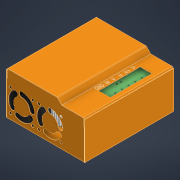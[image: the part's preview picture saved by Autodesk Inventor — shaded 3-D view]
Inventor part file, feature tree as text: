
AUTODESK INVENTOR PART (.ipt)
format: ipt  version: 2022 (Build 260153000, 153)  size: 3,366,912 bytes
history: native  units: in
note: dims shown in document units (in); Inventor stores cm internally (conversion verified against a paired STEP export)
features: other x13, sheet_metal_op x12, sketch x10, plane x2, pattern_linear x2, mirror x1, hole x1, emboss x1, projected_geometry x1
ambient origin geometry x8: Origin, YZ Plane, XZ Plane, XY Plane, X Axis, Y Axis, Z Axis, Center Point
bodies: Solid1 (feature_tree), Solid2 (feature_tree), Solid3 (feature_tree), Solid4 (feature_tree), Solid5 (feature_tree)
feature tree (43):
  other  "Inner Assembly.iam"
  other  "heatsink.ipt:1"
  other  "PCB v1.iam:1::HV servo drive v1 PCB.ipt:1"
  other  "SanAce_9GA_40x20_RBD.ipt:1"
  plane  "Work Plane1"
  sheet_metal_op  "Face1"
  sheet_metal_op  "Flange1"
  sheet_metal_op  "Flange2"
  sketch  "Sketch4"  dims[d4=0.1in]
  sheet_metal_op  "Face3"
  plane  "Work Plane2"
  mirror  "Mirror1"
  sheet_metal_op  "Contour Flange1"
  sketch  "Sketch6"  dims[d6=0.03in]
  hole  "Hole1"  [1 undecoded]
  pattern_linear  "Rectangular Pattern1"  Spacing1=-0.45in  [1 undecoded]
  pattern_linear  "Rectangular Pattern2"  Spacing1=0.12in  [1 undecoded]
  emboss  "Emboss1"
  sketch  "Sketch1"  dims[d0=0.3937in d1=0.06in]
  other  "Plate1"
  sketch  "Sketch2"  dims[d2=0.1in]
  other  "Plate2"
  sheet_metal_op  "Bend1"
  sheet_metal_op  "Corner1"
  sketch  "Sketch3"  dims[d3=1.0in]
  other  "Plate3"
  sheet_metal_op  "Bend2"
  sheet_metal_op  "Corner2"
  other  "Plate5"
  sheet_metal_op  "Bend4"
  sketch  "Sketch5"  dims[d5=0.03in]
  other  "Plate6"
  sheet_metal_op  "Bend5"
  sheet_metal_op  "Corner3"
  sketch  "Sketch7"  dims[d7=0.015in]
  sketch  "Sketch8"  dims[d8=0.06in]
  sketch  "Sketch9"  dims[d9=0.03in]
  projected_geometry  "Projected Loop1"
  sketch  "Sketch10"  dims[d10=1.0in d11=90.0deg d12=0.03in d13=-0.45in d14=0.12in d15=0.03in d16=0.03in d17=0.03in d18=0.015in d19=0.06in d20=0.03in d21=1.0in d22=90.0deg d23=0.03in d24=-0.2in d25=0.12in d26=0.03in d27=0.03in d28=0.2362in d29=0.03in d30=0.03in d31=0.03in d32=0.03in d33=0.03in d34=0.03in d35=0.03in d36=0.03in d37=135.0deg d38=0.5in d39=1.25in d40=0.3937in d41=0.3937in d47=0.005in d48=0.005in d49=0.03in d50=0.03in d51=0.015in d52=0.06in d53=0.03in d54=0.03in d55=0.03in d56=0.015in d57=0.06in d58=0.03in d59=5.037in d60=0.03in d61=0.03in d62=0.12in d63=0.03in d64=0.03in d65=1.2598in d66=1.5748in d67=0.04in d68=0.0394in d69=0.45in d70=0.2983in d71=1.1811in d73=360.0deg d75=0.4in d76=0.1575in d77=0.236in d78=0.119in d79=0.25in d80=0.5635in d81=0.03in d82=0.8108in d83=0.03in d84=0.0in d85=0.7874in d87=1.6142in d88=0.2in d89=0.15in d90=0.15in d91=0.03in d92=0.0in d93=0.0344in d94=3.937in d96=0.3in d97=0.31in d98=0.31in d99=0.02in d100=0.03in d101=0.0in d102=0.6693in d103=2.3622in d104=0.03in d105=0.0in d106=0.001in d107=0.0in]
  other  "Cut1"
  other  "Cut2"
  other  "Cut3"
  other  "Cut4"
note: 3 required parameter values undecoded (feature->parameter linkage not recoverable at this tier; creation-order binding heuristic only, values carry confidence <= 0.55)
